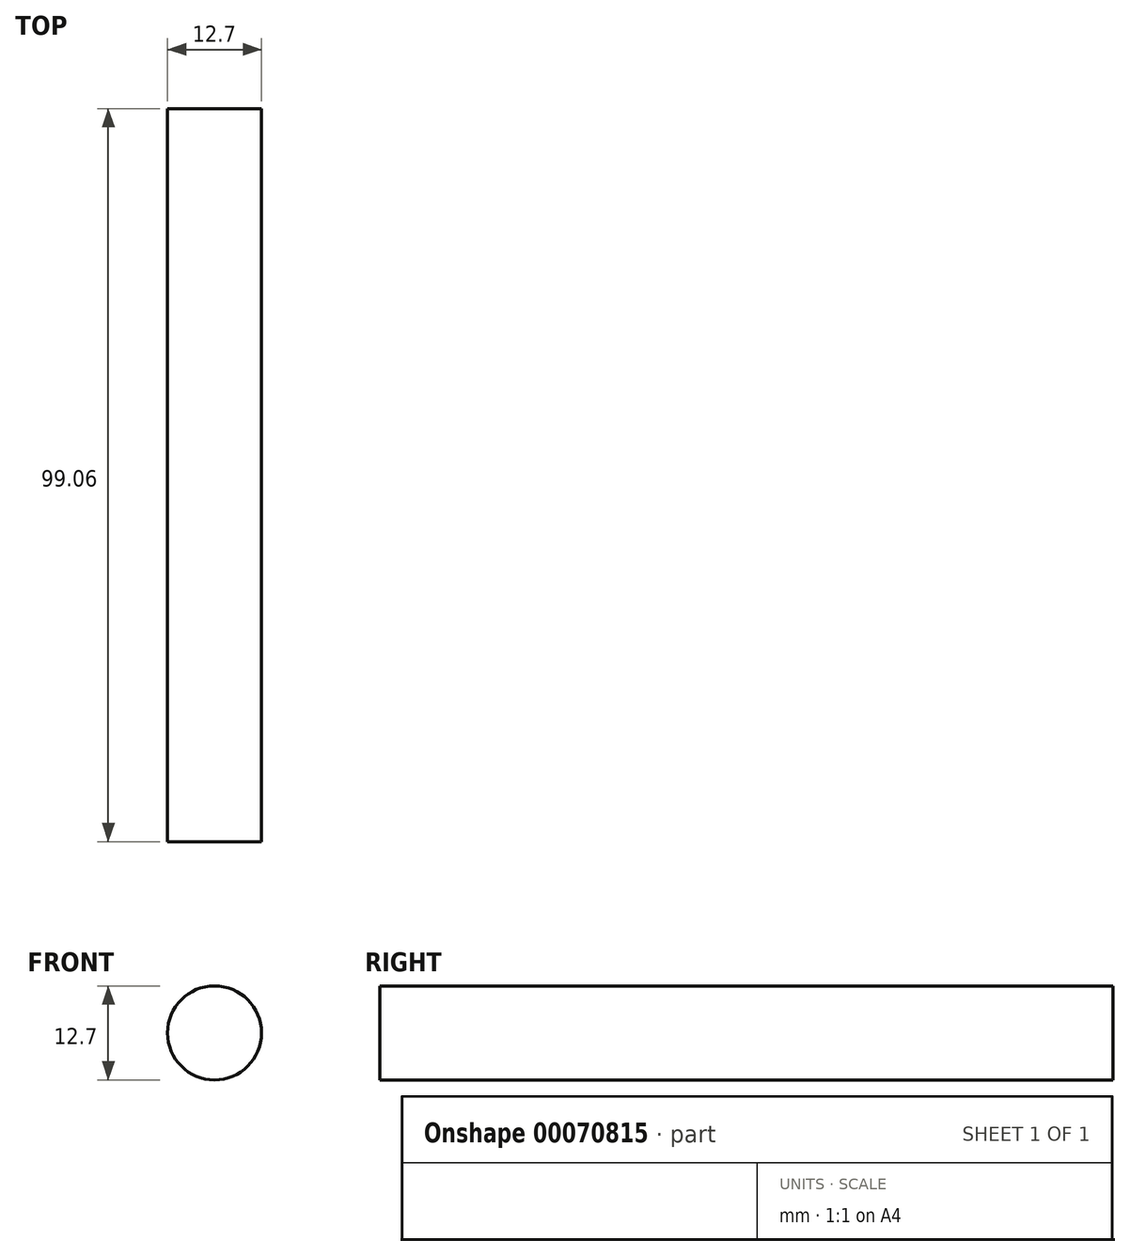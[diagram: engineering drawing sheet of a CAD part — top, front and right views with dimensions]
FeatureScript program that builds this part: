
annotation { "Feature Type Name" : "Feature", "Feature Type Description" : "" }
export const myFeature = defineFeature(function(context is Context, id is Id, definition is map)
    precondition{}
    {
        {
            var Q0;
            Q0=qCreatedBy(makeId("Front.planeOp"),FACE);
            var sketch = newSketch(context, id + "F0", { "sketchPlane" : qUnion([Q0])});
            skCircle(sketch, "E0", {"center": v(0, 0) * mm, "radius": 6.35 * mm});
            skSolve(sketch);
        }
        {
            var Q0;
            Q0 = qSketchRegion(id + "F0", true);
            extrude(context, id + "F1", {"entities" : qUnion([Q0]), "depth" : 99.06 * mm});
        }
    });
